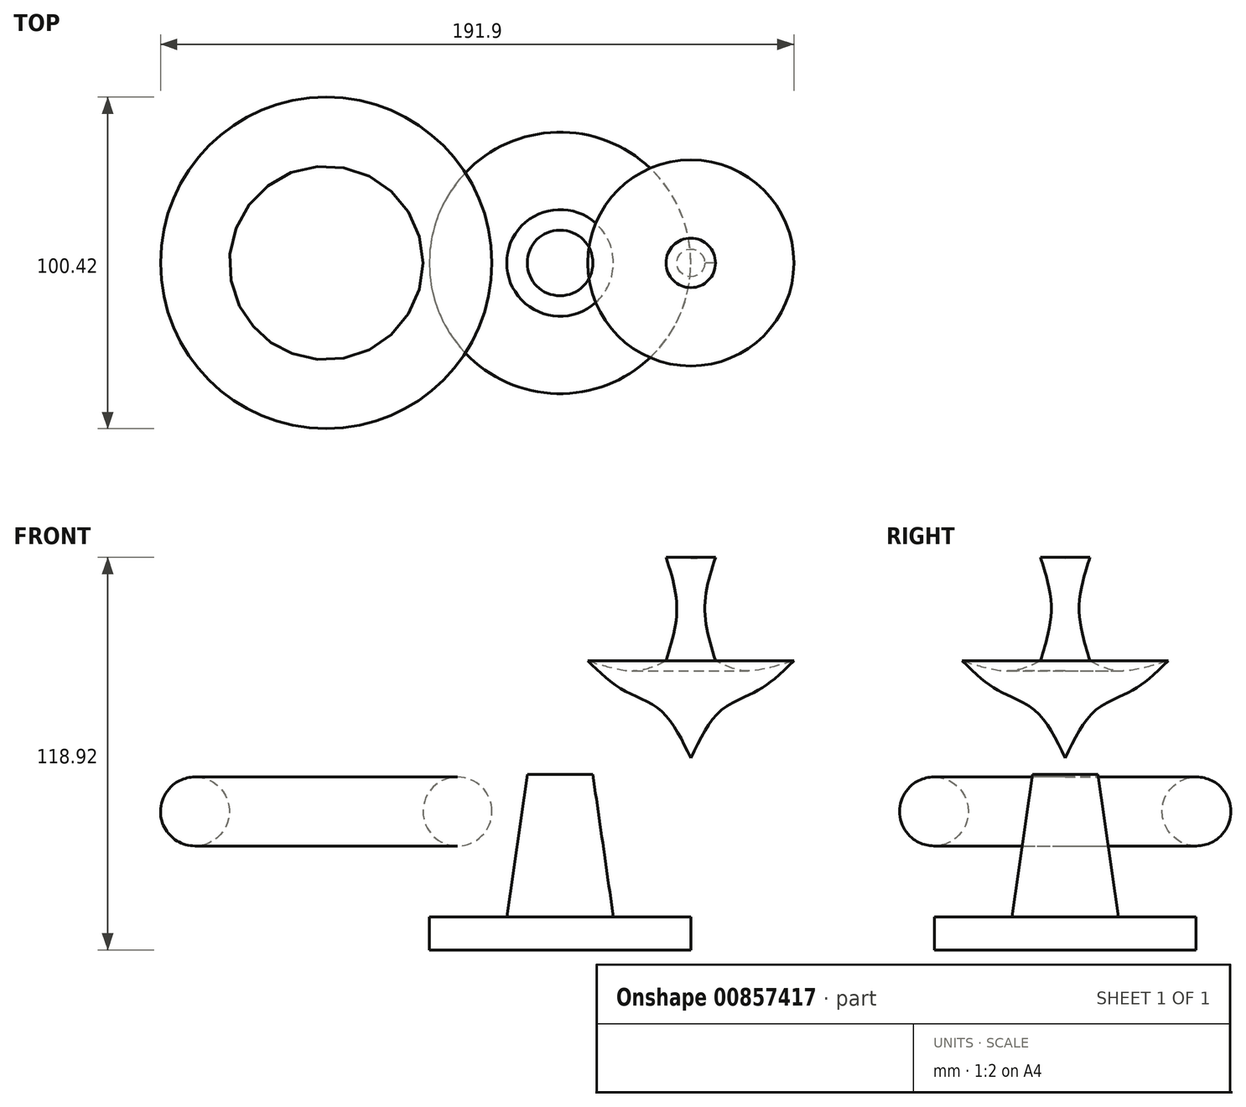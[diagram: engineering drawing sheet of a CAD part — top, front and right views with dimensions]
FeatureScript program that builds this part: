
annotation { "Feature Type Name" : "Feature", "Feature Type Description" : "" }
export const myFeature = defineFeature(function(context is Context, id is Id, definition is map)
    precondition{}
    {
        {
            var Q0;
            Q0=qCreatedBy(makeId("Front.planeOp"),FACE);
            var sketch = newSketch(context, id + "F0", { "sketchPlane" : qUnion([Q0])});
            skLineSegment(sketch, "E0", {"start": v(0, 60.6) * mm, "end": v(0, 0) * mm});
            skLineSegment(sketch, "E1", {"start": v(-7.49, 60.82) * mm, "end": v(0, 60.6) * mm});
            skFitSpline(sketch, "E2", {"points": [v(-7.49, 60.82) * mm, v(-4.22, 45.54) * mm, v(-7.49, 29.52) * mm], "startDerivative": vector(9.83, -30.72) * mm, "endDerivative": vector(-9.75, -31.88) * mm});
            skFitSpline(sketch, "E3", {"points": [v(-31.23, 29.52) * mm, v(-20.68, 20.72) * mm, v(-9.19, 14.45) * mm, v(0, 0) * mm], "startDerivative": vector(30.9, -30.45) * mm, "endDerivative": vector(22.08, -46.25) * mm});
            skFitSpline(sketch, "E4", {"points": [v(-31.23, 29.52) * mm, v(-16.5, 26.47) * mm, v(-7.49, 29.52) * mm], "startDerivative": vector(28.14, -8.92) * mm, "endDerivative": vector(19, 9.62) * mm});
            skSolve(sketch);
        }
        {
            var Q0;
            Q0=makeQuery(id+"F0.imprint","IMPRINT",FACE,{"disambiguationData":[TD([[makeQuery(id+"F0.imprint","IMPRINT",EDGE,{"derivedFrom":sQuery(id+"F0.wireOp",EDGE,"E0")}),-1.0]])]});
            var Q1;
            Q1=sQuery(id+"F0.wireOp",EDGE,"E0");
            revolve(context, id + "F1", {"surfaceOperationType" : NewSurfaceOperationType.NEW, "entities" : qUnion([Q0]), "axis" : qUnion([Q1]), "revolveType" : RevolveType.FULL});
        }
        {
            var Q0;
            Q0=qCreatedBy(makeId("Front.planeOp"),FACE);
            var sketch = newSketch(context, id + "F2", { "sketchPlane" : qUnion([Q0])});
            skLineSegment(sketch, "E5.bottom", {"start": v(-39.62, -4.97) * mm, "end": v(0, -4.97) * mm});
            skLineSegment(sketch, "E5.top", {"start": v(-39.62, -58.1) * mm, "end": v(0, -58.1) * mm});
            skLineSegment(sketch, "E5.left", {"start": v(-39.62, -4.97) * mm, "end": v(-39.62, -58.1) * mm});
            skLineSegment(sketch, "E5.right", {"start": v(0, -4.97) * mm, "end": v(0, -58.1) * mm});
            skLineSegment(sketch, "E6", {"start": v(-29.67, -4.97) * mm, "end": v(-23.46, -48.16) * mm});
            skLineSegment(sketch, "E7", {"start": v(0, -48.16) * mm, "end": v(-23.46, -48.16) * mm});
            skSolve(sketch);
        }
        {
            var Q0;
            {var subQ1=sQuery(id+"F2.wireOp",EDGE,"E5.top");Q0=makeQuery(id+"F2.imprint","IMPRINT",FACE,{"disambiguationData":[TD([[makeQuery(id+"F2.imprint","IMPRINT",EDGE,{"derivedFrom":subQ1}),1.0]])]});}
            var Q1;
            Q1=sQuery(id+"F2.wireOp",EDGE,"E5.left");
            revolve(context, id + "F3", {"surfaceOperationType" : NewSurfaceOperationType.NEW, "entities" : qUnion([Q0]), "axis" : qUnion([Q1]), "revolveType" : RevolveType.FULL});
        }
        {
            var Q0;
            Q0=qCreatedBy(makeId("Front.planeOp"),FACE);
            var sketch = newSketch(context, id + "F4", { "sketchPlane" : qUnion([Q0])});
            skCircle(sketch, "E8", {"center": v(-150.23, -16.16) * mm, "radius": 10.44 * mm});
            skLineSegment(sketch, "E9", {"start": v(-110.46, -6.84) * mm, "end": v(-110.46, -28.28) * mm});
            skSolve(sketch);
        }
        {
            var Q0;
            Q0=makeQuery(id+"F4.imprint","IMPRINT",FACE,{"disambiguationData":[TD([[makeQuery(id+"F4.imprint","IMPRINT",EDGE,{"derivedFrom":sQuery(id+"F4.wireOp",EDGE,"E8")}),1.0]])]});
            var Q1;
            Q1=sQuery(id+"F4.wireOp",EDGE,"E9");
            revolve(context, id + "F5", {"surfaceOperationType" : NewSurfaceOperationType.NEW, "entities" : qUnion([Q0]), "axis" : qUnion([Q1]), "revolveType" : RevolveType.FULL});
        }
    });
